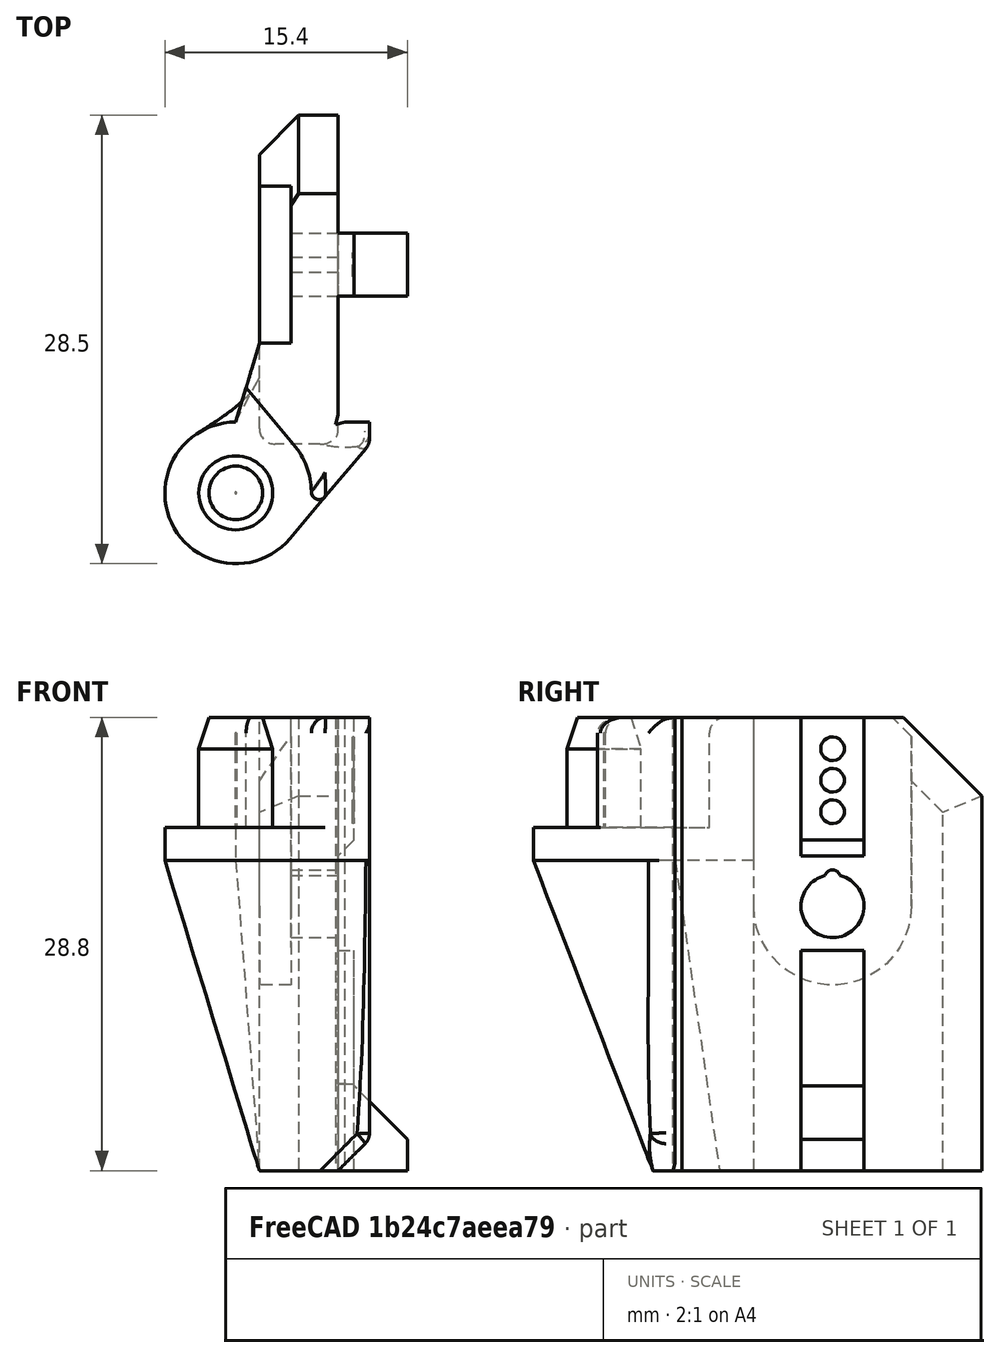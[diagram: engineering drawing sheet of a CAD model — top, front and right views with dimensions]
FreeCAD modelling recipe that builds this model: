
FCSTD DOCUMENT  (FreeCAD 0.18R14555 (Git shallow))
Label: hingle-bottom
License: All rights reserved
LicenseURL: http://en.wikipedia.org/wiki/All_rights_reserved
objects: Part::Cut×6, Part::Feature×5, Part::Box×5, Part::Chamfer×2, App::Part×1, Part::MultiCommon×1, Part::MultiFuse×1
note: 20 computed .brp shape members not serialized (recipe doc carries the construction recipe); baked Part::Feature solids carry a one-line shape summary decoded from their .brp

FEATURE [Part::Feature] Part__Feature002  label="rambo_hinge_lower"
  Placement = pos=(0,0,21.8) rot=(0,0,1;0rad)
  shape: bbox 15.9 x 28.5 x 29.26 mm, 61 faces (baked)
FEATURE [App::Part] rambo_hinge_lower_v1  label="rambo_hinge_lower v1"
  Group = -> [Part__Feature002]
  Origin = -> Origin002
FEATURE [Part::Box] Box007  label="Cube007"
  AttacherType = Attacher::AttachEngine3D
  Height = 5.5
  Length = 10
  Placement = pos=(6.5,9.5,0) rot=(0,0,1;0rad)
  Width = 3
FEATURE [Part::Box] Box008  label="Cube008"
  AttacherType = Attacher::AttachEngine3D
  Height = 5.5
  Length = 10
  Placement = pos=(6.5,16.5,0) rot=(0,0,1;0rad)
  Width = 3
FEATURE [Part::Cut] Cut001008
  Base = -> Part__Feature002
  Tool = -> Box007
FEATURE [Part::Cut] Cut001009
  Base = -> Cut001008
  Tool = -> Box008
FEATURE [Part::Feature] Part__Feature009  label="T-slot-align-cut002"
  Placement = pos=(16.5,19.73,5.5) rot=(0.57735,-0.57735,0.57735;2.0944rad)
  shape: bbox 5.002 x 10.25 x 40 mm, 10 faces (baked)
FEATURE [Part::Cut] Cut001010
  Base = -> Cut001009
  Tool = -> Part__Feature009
FEATURE [Part::Box] Box009  label="Cube009"
  AttacherType = Attacher::AttachEngine3D
  Height = 9
  Length = 2
  Placement = pos=(5.5,8,12.5) rot=(0,0,1;0rad)
  Width = 11
FEATURE [Part::Chamfer] Chamfer001
  Base = -> Box009
  Edges = 1 edges r=1: [Edge2]
  Placement = pos=(1,0,0.5) rot=(0,0,1;0rad)
FEATURE [Part::Cut] Cut001011
  Base = -> Cut001010
  Tool = -> Chamfer001
FEATURE [Part::Box] Box010  label="Cube010"
  AttacherType = Attacher::AttachEngine3D
  Height = 5.5
  Length = 10
  Placement = pos=(6.5,9,0) rot=(0,0,1;0rad)
  Width = 10
FEATURE [Part::Box] Box011  label="Cube011"
  AttacherType = Attacher::AttachEngine3D
  Height = 7
  Length = 10
  Placement = pos=(6.5,9,14) rot=(0,0,1;0rad)
  Width = 10
FEATURE [Part::MultiCommon] Common
  Placement = pos=(-0.5,0,0) rot=(0,0,1;0rad)
  Shapes = -> [Box010,Cut001011]
FEATURE [Part::Feature] Part__Feature010  label="m5-to-m4-bolt-hole002"
  Placement = pos=(6.5,14.5,16.8) rot=(0,0,-1;1.5708rad)
  shape: bbox 3 x 6 x 6 mm, 5 faces (baked)
FEATURE [Part::Feature] Part__Feature  label="t-slot-align"
  Placement = pos=(6.5,9.28,1.4e-15) rot=(0.57735,0.57735,0.57735;4.18879rad)
  shape: bbox 5.002 x 10.45 x 60 mm, 10 faces (baked)
FEATURE [Part::Cut] Cut
  Base = -> Part__Feature002
  Tool = -> Part__Feature
FEATURE [Part::Chamfer] Chamfer
  Base = -> Box011
  Edges = 1 edges r=1: [Edge2]
FEATURE [Part::Cut] Cut001012
  Base = -> Cut
  Tool = -> Chamfer
FEATURE [Part::MultiFuse] Fusion
  Shapes = -> [Cut001012,Common,Part__Feature010]
FEATURE [Part::Feature] Fusion001
  shape: bbox 15.4 x 28.5 x 29.26 mm, 62 faces (baked)
